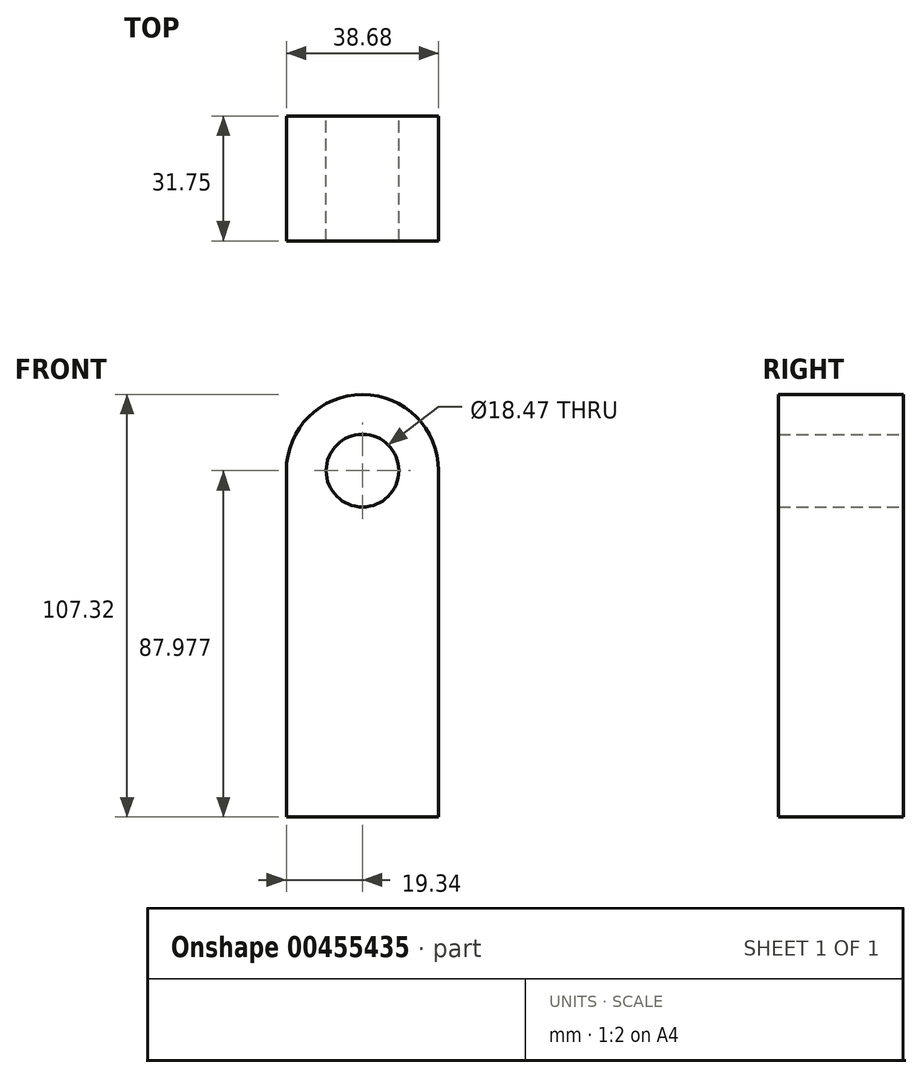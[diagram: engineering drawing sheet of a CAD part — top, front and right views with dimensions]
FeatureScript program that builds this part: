
annotation { "Feature Type Name" : "Feature", "Feature Type Description" : "" }
export const myFeature = defineFeature(function(context is Context, id is Id, definition is map)
    precondition{}
    {
        {
            var Q0;
            Q0=qCreatedBy(makeId("Front.planeOp"),FACE);
            var sketch = newSketch(context, id + "F0", { "sketchPlane" : qUnion([Q0])});
            skLineSegment(sketch, "E0.bottom", {"start": v(19.34, -43.99) * mm, "end": v(-19.34, -43.99) * mm});
            skLineSegment(sketch, "E0.left", {"start": v(19.34, -43.99) * mm, "end": v(19.34, 43.99) * mm});
            skLineSegment(sketch, "E0.right", {"start": v(-19.34, -43.99) * mm, "end": v(-19.34, 43.99) * mm});
            skPoint(sketch, "E0.middle", {"position": v(0, 0) * mm});
            skCircle(sketch, "E1", {"center": v(0, 43.99) * mm, "radius": 9.23 * mm});
            skArc(sketch, "E2", {"start": v(19.34, 43.99) * mm, "mid": v(0, 63.33) * mm, "end": v(-19.34, 43.99) * mm});
            skSolve(sketch);
        }
        {
            var Q0;
            Q0=makeQuery(id+"F0.imprint","IMPRINT",FACE,{"disambiguationData":[TD([[makeQuery(id+"F0.imprint","IMPRINT",EDGE,{"derivedFrom":sQuery(id+"F0.wireOp",EDGE,"E0.bottom")}),-1.0]])]});
            extrude(context, id + "F1", {"entities" : qUnion([Q0]), "depth" : 31.75 * mm});
        }
    });
